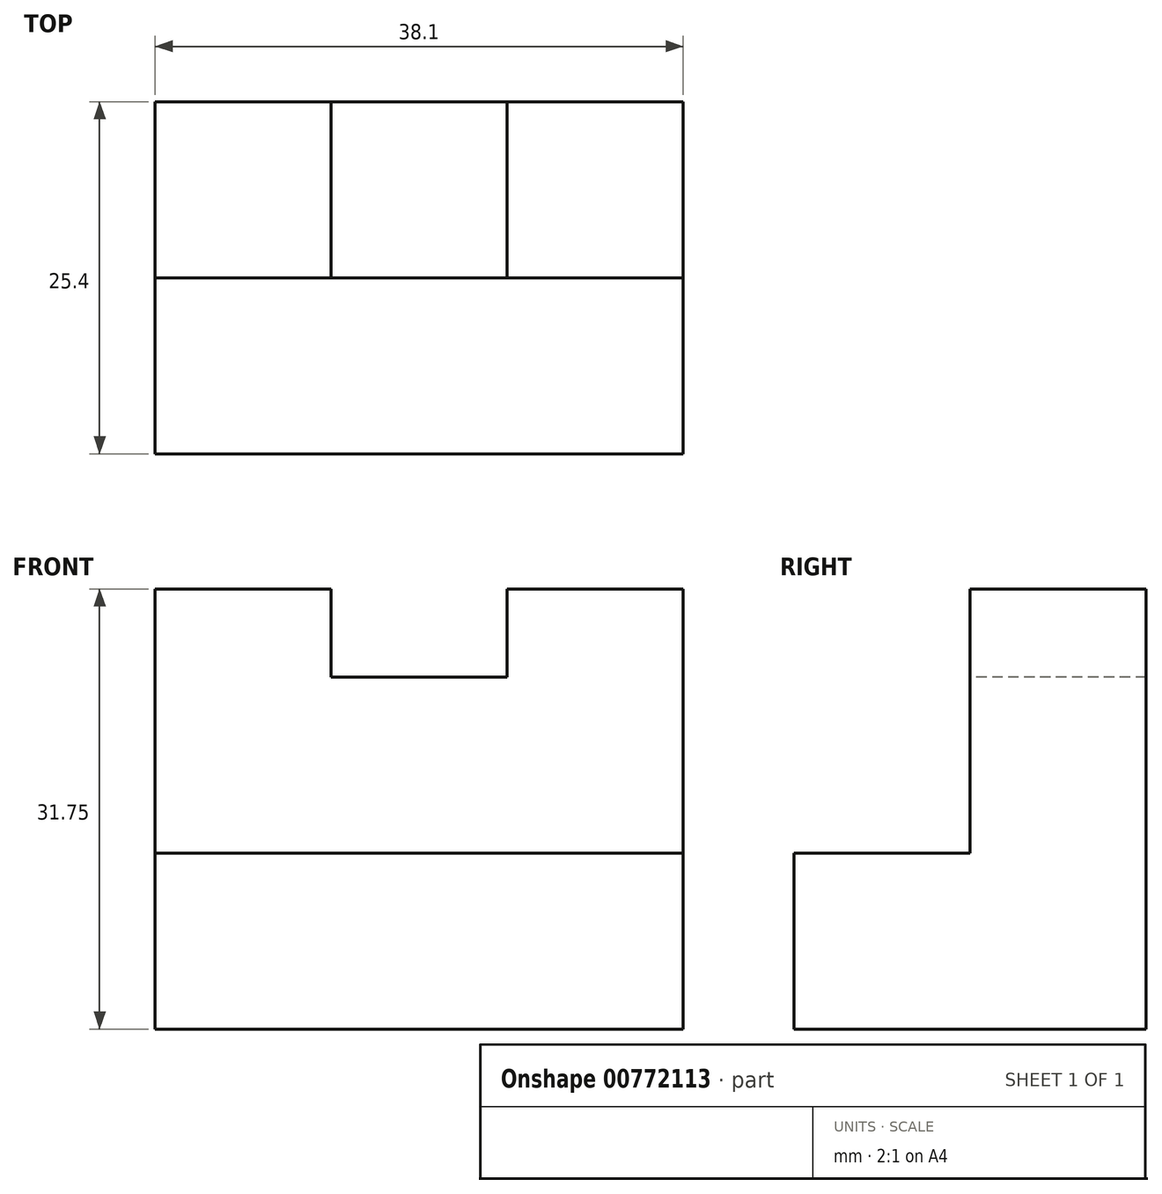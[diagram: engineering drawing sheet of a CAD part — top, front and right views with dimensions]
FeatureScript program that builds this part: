
annotation { "Feature Type Name" : "Feature", "Feature Type Description" : "" }
export const myFeature = defineFeature(function(context is Context, id is Id, definition is map)
    precondition{}
    {
        {
            var Q0;
            Q0=qCreatedBy(makeId("Front.planeOp"),FACE);
            var sketch = newSketch(context, id + "F0", { "sketchPlane" : qUnion([Q0])});
            skLineSegment(sketch, "E0", {"start": v(0, 0) * mm, "end": v(38.1, 0) * mm});
            skLineSegment(sketch, "E1", {"start": v(38.1, 0) * mm, "end": v(38.1, 31.75) * mm});
            skLineSegment(sketch, "E2", {"start": v(38.1, 31.75) * mm, "end": v(0, 31.75) * mm});
            skLineSegment(sketch, "E3", {"start": v(0, 31.75) * mm, "end": v(0, 0) * mm});
            skSolve(sketch);
        }
        {
            var Q0;
            Q0 = qSketchRegion(id + "F0", true);
            extrude(context, id + "F1", {"entities" : qUnion([Q0]), "depth" : 25.4 * mm, "offsetDistance" : 25.4 * mm});
        }
        {
            var Q0;
            Q0=makeQuery(id+"F1.opExtrude","SWEPT_FACE",FACE,{"disambiguationData":[OSD([sQuery(id+"F0.wireOp",EDGE,"E1")])]});
            var sketch = newSketch(context, id + "F2", { "sketchPlane" : qUnion([Q0])});
            skLineSegment(sketch, "E4", {"start": v(-25.4, 0) * mm, "end": v(-25.4, 12.7) * mm});
            skLineSegment(sketch, "E5", {"start": v(-25.4, 12.7) * mm, "end": v(-12.7, 12.7) * mm});
            skLineSegment(sketch, "E6", {"start": v(-12.7, 12.7) * mm, "end": v(-12.7, 31.75) * mm});
            skSolve(sketch);
        }
        {
            var Q0;
            {var subQ0=sQuery(id+"F2.wireOp",EDGE,"E5");Q0=makeQuery(id+"F2.imprint","IMPRINT",FACE,{"disambiguationData":[TD([[makeQuery(id+"F2.imprint","IMPRINT",EDGE,{"derivedFrom":subQ0}),1.0]])]});}
            extrude(context, id + "F3", {"entities" : qUnion([Q0]), "operationType" : NewBodyOperationType.REMOVE, "oppositeDirection" : true, "depth" : 38.1 * mm, "offsetDistance" : 25.4 * mm});
        }
        {
            var Q0;
            Q0=makeQuery(id+"F3.boolean.opBoolean","COPY",FACE,{"derivedFrom":makeQuery(id+"F3.opExtrude","SWEPT_FACE",FACE,{"disambiguationData":[OSD([sQuery(id+"F2.wireOp",EDGE,"E6")])]})});
            var sketch = newSketch(context, id + "F4", { "sketchPlane" : qUnion([Q0])});
            skLineSegment(sketch, "E7", {"start": v(38.1, 31.75) * mm, "end": v(25.4, 31.75) * mm});
            skLineSegment(sketch, "E8", {"start": v(25.4, 31.75) * mm, "end": v(25.4, 25.4) * mm});
            skLineSegment(sketch, "E9", {"start": v(25.4, 25.4) * mm, "end": v(12.7, 25.4) * mm});
            skLineSegment(sketch, "E10", {"start": v(12.7, 25.4) * mm, "end": v(12.7, 31.75) * mm});
            skLineSegment(sketch, "E11", {"start": v(12.7, 31.75) * mm, "end": v(0, 31.75) * mm});
            skSolve(sketch);
        }
        {
            var Q0;
            {var subQ0=sQuery(id+"F4.wireOp",EDGE,"E8");Q0=makeQuery(id+"F4.imprint","IMPRINT",FACE,{"disambiguationData":[TD([[makeQuery(id+"F4.imprint","IMPRINT",EDGE,{"derivedFrom":subQ0}),-1.0]])]});}
            extrude(context, id + "F5", {"entities" : qUnion([Q0]), "operationType" : NewBodyOperationType.REMOVE, "oppositeDirection" : true, "depth" : 25.4 * mm, "offsetDistance" : 25.4 * mm});
        }
    });
